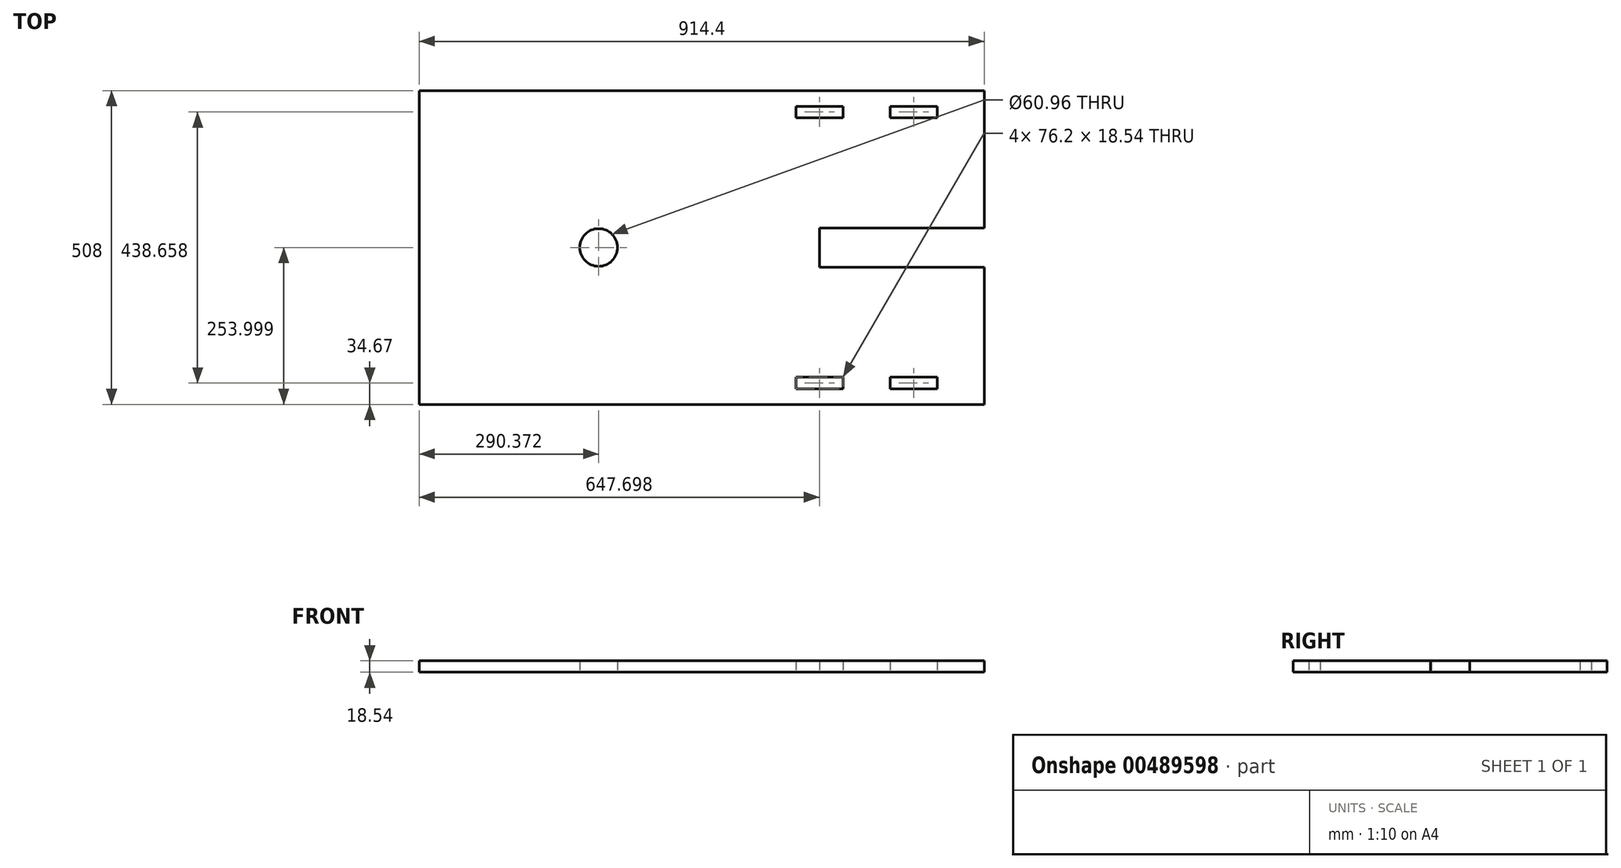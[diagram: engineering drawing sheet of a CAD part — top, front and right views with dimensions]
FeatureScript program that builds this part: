
annotation { "Feature Type Name" : "Feature", "Feature Type Description" : "" }
export const myFeature = defineFeature(function(context is Context, id is Id, definition is map)
    precondition{}
    {
        {
            var Q0;
            Q0=qCreatedBy(makeId("Top.planeOp"),FACE);
            var sketch = newSketch(context, id + "F0", { "sketchPlane" : qUnion([Q0])});
            skLineSegment(sketch, "E0.bottom", {"start": v(-1646.8, 852.39) * mm, "end": v(-732.4, 852.39) * mm});
            skLineSegment(sketch, "E0.top", {"start": v(-1646.8, 344.39) * mm, "end": v(-732.4, 344.39) * mm});
            skLineSegment(sketch, "E0.left", {"start": v(-1646.8, 852.39) * mm, "end": v(-1646.8, 344.39) * mm});
            skLineSegment(sketch, "E0.right", {"start": v(-732.4, 852.39) * mm, "end": v(-732.4, 369.79) * mm});
            skLineSegment(sketch, "E1", {"start": v(-1646.8, 547.59) * mm, "end": v(-1646.8, 344.39) * mm});
            skLineSegment(sketch, "E2.bottom", {"start": v(-732.4, 566.64) * mm, "end": v(-999.1, 566.64) * mm});
            skLineSegment(sketch, "E2.top", {"start": v(-732.4, 630.14) * mm, "end": v(-999.1, 630.14) * mm});
            skLineSegment(sketch, "E2.left", {"start": v(-732.4, 566.64) * mm, "end": v(-732.4, 630.14) * mm});
            skLineSegment(sketch, "E2.right", {"start": v(-999.1, 566.64) * mm, "end": v(-999.1, 630.14) * mm});
            skPoint(sketch, "E3.orphan", {"position": v(-1646.8, 598.39) * mm});
            skPoint(sketch, "E4.end.orphan", {"position": v(-732.4, 598.39) * mm});
            skPoint(sketch, "E5.end.orphan", {"position": v(-1380.1, 369.79) * mm});
            skPoint(sketch, "E6.end.orphan", {"position": v(-1227.7, 369.79) * mm});
            skPoint(sketch, "E7.end.orphan", {"position": v(-1303.9, 369.79) * mm});
            skPoint(sketch, "E8.end.orphan", {"position": v(-1151.5, 369.79) * mm});
            skLineSegment(sketch, "E9", {"start": v(-808.6, 369.79) * mm, "end": v(-884.8, 369.79) * mm});
            skLineSegment(sketch, "E10", {"start": v(-808.6, 826.99) * mm, "end": v(-884.8, 826.99) * mm});
            skLineSegment(sketch, "E11", {"start": v(-732.4, 826.99) * mm, "end": v(-732.4, 808.45) * mm});
            skLineSegment(sketch, "E12", {"start": v(-808.6, 808.45) * mm, "end": v(-808.6, 826.99) * mm});
            skLineSegment(sketch, "E13", {"start": v(-808.6, 826.99) * mm, "end": v(-808.6, 808.45) * mm});
            skLineSegment(sketch, "E14", {"start": v(-808.6, 826.99) * mm, "end": v(-732.4, 826.99) * mm});
            skLineSegment(sketch, "E15", {"start": v(-808.6, 808.45) * mm, "end": v(-884.8, 808.45) * mm});
            skLineSegment(sketch, "E16", {"start": v(-884.8, 808.45) * mm, "end": v(-884.8, 826.99) * mm});
            skLineSegment(sketch, "E17", {"start": v(-884.8, 826.99) * mm, "end": v(-808.6, 826.99) * mm});
            skLineSegment(sketch, "E18", {"start": v(-961, 808.45) * mm, "end": v(-961, 826.99) * mm});
            skLineSegment(sketch, "E19", {"start": v(-961, 808.45) * mm, "end": v(-1037.2, 808.45) * mm});
            skLineSegment(sketch, "E20", {"start": v(-1037.2, 808.45) * mm, "end": v(-1037.2, 826.99) * mm});
            skLineSegment(sketch, "E21", {"start": v(-1037.2, 826.99) * mm, "end": v(-961, 826.99) * mm});
            skLineSegment(sketch, "E22", {"start": v(-732.4, 344.39) * mm, "end": v(-732.4, 369.79) * mm});
            skLineSegment(sketch, "E23", {"start": v(-808.6, 388.33) * mm, "end": v(-808.6, 369.79) * mm});
            skLineSegment(sketch, "E24", {"start": v(-808.6, 388.33) * mm, "end": v(-884.8, 388.33) * mm});
            skLineSegment(sketch, "E25", {"start": v(-884.8, 388.33) * mm, "end": v(-884.8, 369.79) * mm});
            skLineSegment(sketch, "E26", {"start": v(-884.8, 369.79) * mm, "end": v(-808.6, 369.79) * mm});
            skLineSegment(sketch, "E27", {"start": v(-961, 369.79) * mm, "end": v(-961, 388.33) * mm});
            skLineSegment(sketch, "E28", {"start": v(-961, 388.33) * mm, "end": v(-1037.2, 388.33) * mm});
            skLineSegment(sketch, "E29", {"start": v(-1037.2, 388.33) * mm, "end": v(-1037.2, 369.79) * mm});
            skLineSegment(sketch, "E30", {"start": v(-1037.2, 369.79) * mm, "end": v(-961, 369.79) * mm});
            skLineSegment(sketch, "E31.trimOffspring", {"start": v(-961, 369.79) * mm, "end": v(-1037.2, 369.79) * mm});
            skPoint(sketch, "E32.end.orphan", {"position": v(-1113.4, 808.45) * mm});
            skLineSegment(sketch, "E33.trimOffspring", {"start": v(-961, 826.99) * mm, "end": v(-1037.2, 826.99) * mm});
            skCircle(sketch, "E34", {"center": v(-1356.43, 598.39) * mm, "radius": 30.48 * mm});
            skPoint(sketch, "E35.orphan", {"position": v(-999.1, 598.39) * mm});
            skSolve(sketch);
        }
        {
            var Q0;
            {var subQ0=sQuery(id+"F0.wireOp",EDGE,"E0.right");Q0=makeQuery(id+"F0.imprint","IMPRINT",FACE,{"disambiguationData":[TD([[makeQuery(id+"F0.imprint","IMPRINT",EDGE,{"derivedFrom":subQ0}),-1.0]])]});}
            var Q1;
            Q1=makeQuery(id+"F0.imprint","IMPRINT",FACE,{"disambiguationData":[TD([[makeQuery(id+"F0.imprint","IMPRINT",EDGE,{"derivedFrom":sQuery(id+"F0.wireOp",EDGE,"E1")}),1.0]])]});
            extrude(context, id + "F1", {"entities" : qUnion([Q0, Q1]), "depth" : 18.54 * mm, "offsetDistance" : 25.4 * mm});
        }
        {
            var Q0;
            {var subQ3=sQuery(id+"F0.wireOp",EDGE,"E0.bottom");Q0=makeQuery(id+"F0.imprint","IMPRINT",FACE,{"disambiguationData":[TD([[makeQuery(id+"F0.imprint","IMPRINT",EDGE,{"derivedFrom":subQ3}),-1.0]])]});}
            extrude(context, id + "F2", {"entities" : qUnion([Q0]), "operationType" : NewBodyOperationType.ADD, "depth" : 18.54 * mm, "offsetDistance" : 25.4 * mm});
        }
    });
